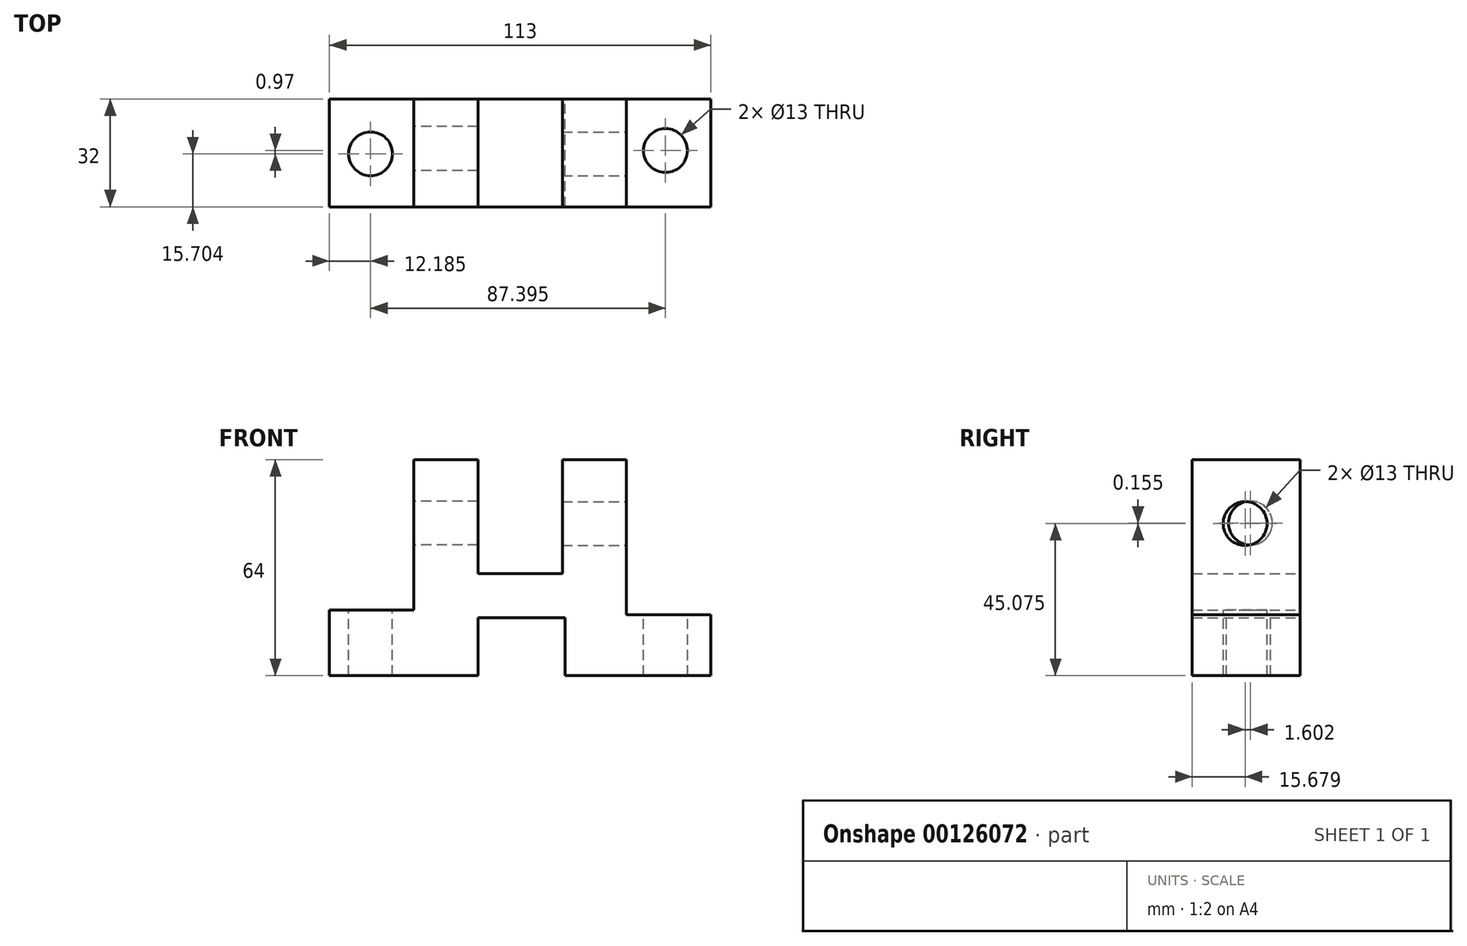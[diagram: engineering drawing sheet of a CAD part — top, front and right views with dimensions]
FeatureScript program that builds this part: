
annotation { "Feature Type Name" : "Feature", "Feature Type Description" : "" }
export const myFeature = defineFeature(function(context is Context, id is Id, definition is map)
    precondition{}
    {
        {
            var Q0;
            Q0=qCreatedBy(makeId("Front.planeOp"),FACE);
            var sketch = newSketch(context, id + "F0", { "sketchPlane" : qUnion([Q0])});
            skLineSegment(sketch, "E0", {"start": v(0, 0) * mm, "end": v(44, 0) * mm});
            skLineSegment(sketch, "E1", {"start": v(44, 0) * mm, "end": v(44, 17.17) * mm});
            skLineSegment(sketch, "E2", {"start": v(44, 17.17) * mm, "end": v(69.76, 17.17) * mm});
            skLineSegment(sketch, "E3", {"start": v(69.76, 17.17) * mm, "end": v(69.76, 0) * mm});
            skLineSegment(sketch, "E4", {"start": v(69.76, 0) * mm, "end": v(113, 0) * mm});
            skLineSegment(sketch, "E5", {"start": v(113, 0) * mm, "end": v(113, 18.09) * mm});
            skLineSegment(sketch, "E6", {"start": v(113, 18.09) * mm, "end": v(88, 18.09) * mm});
            skLineSegment(sketch, "E7", {"start": v(88, 18.09) * mm, "end": v(88, 64) * mm});
            skLineSegment(sketch, "E8", {"start": v(88, 64) * mm, "end": v(69, 64) * mm});
            skLineSegment(sketch, "E9", {"start": v(69, 64) * mm, "end": v(69, 30.17) * mm});
            skLineSegment(sketch, "E10", {"start": v(69, 30.17) * mm, "end": v(44, 30.17) * mm});
            skLineSegment(sketch, "E11", {"start": v(44, 30.17) * mm, "end": v(44, 64) * mm});
            skLineSegment(sketch, "E12", {"start": v(44, 64) * mm, "end": v(25, 64) * mm});
            skLineSegment(sketch, "E13", {"start": v(25, 64) * mm, "end": v(25, 19.49) * mm});
            skLineSegment(sketch, "E14", {"start": v(25, 19.49) * mm, "end": v(0, 19.49) * mm});
            skLineSegment(sketch, "E15", {"start": v(0, 19.49) * mm, "end": v(0, 0) * mm});
            skSolve(sketch);
        }
        {
            var Q0;
            Q0 = qSketchRegion(id + "F0", true);
            extrude(context, id + "F1", {"entities" : qUnion([Q0]), "depth" : 32 * mm});
        }
        {
            var Q0;
            Q0=makeQuery(id+"F1.opExtrude","SWEPT_FACE",FACE,{"disambiguationData":[OSD([sQuery(id+"F0.wireOp",EDGE,"E6")])]});
            var sketch = newSketch(context, id + "F2", { "sketchPlane" : qUnion([Q0])});
            skCircle(sketch, "E16", {"center": v(99.58, -15.33) * mm, "radius": 6.5 * mm});
            skSolve(sketch);
        }
        {
            var Q0;
            Q0=makeQuery(id+"F2.imprint","IMPRINT",FACE,{"disambiguationData":[TD([[makeQuery(id+"F2.imprint","IMPRINT",EDGE,{"derivedFrom":sQuery(id+"F2.wireOp",EDGE,"E16")}),1.0]])]});
            extrude(context, id + "F3", {"entities" : qUnion([Q0]), "operationType" : NewBodyOperationType.REMOVE, "oppositeDirection" : true, "depth" : 25 * mm});
        }
        {
            var Q0;
            Q0=makeQuery(id+"F1.opExtrude","SWEPT_FACE",FACE,{"disambiguationData":[OSD([sQuery(id+"F0.wireOp",EDGE,"E14")])]});
            var sketch = newSketch(context, id + "F4", { "sketchPlane" : qUnion([Q0])});
            skCircle(sketch, "E17", {"center": v(12.19, -16.3) * mm, "radius": 6.5 * mm});
            skSolve(sketch);
        }
        {
            var Q0;
            Q0=makeQuery(id+"F4.imprint","IMPRINT",FACE,{"disambiguationData":[TD([[makeQuery(id+"F4.imprint","IMPRINT",EDGE,{"derivedFrom":sQuery(id+"F4.wireOp",EDGE,"E17")}),1.0]])]});
            extrude(context, id + "F5", {"entities" : qUnion([Q0]), "operationType" : NewBodyOperationType.REMOVE, "oppositeDirection" : true, "depth" : 25 * mm});
        }
        {
            var Q0;
            Q0=makeQuery(id+"F1.opExtrude","SWEPT_FACE",FACE,{"disambiguationData":[OSD([sQuery(id+"F0.wireOp",EDGE,"E7")])]});
            var sketch = newSketch(context, id + "F6", { "sketchPlane" : qUnion([Q0])});
            skCircle(sketch, "E18", {"center": v(-16.32, 45.08) * mm, "radius": 6.5 * mm});
            skSolve(sketch);
        }
        {
            var Q0;
            Q0=makeQuery(id+"F6.imprint","IMPRINT",FACE,{"disambiguationData":[TD([[makeQuery(id+"F6.imprint","IMPRINT",EDGE,{"derivedFrom":sQuery(id+"F6.wireOp",EDGE,"E18")}),1.0]])]});
            extrude(context, id + "F7", {"entities" : qUnion([Q0]), "operationType" : NewBodyOperationType.REMOVE, "oppositeDirection" : true, "depth" : 25 * mm});
        }
        {
            var Q0;
            Q0=makeQuery(id+"F1.opExtrude","SWEPT_FACE",FACE,{"disambiguationData":[OSD([sQuery(id+"F0.wireOp",EDGE,"E13")])]});
            var sketch = newSketch(context, id + "F8", { "sketchPlane" : qUnion([Q0])});
            skCircle(sketch, "E19", {"center": v(14.72, 45.23) * mm, "radius": 6.5 * mm});
            skSolve(sketch);
        }
        {
            var Q0;
            Q0 = qSketchRegion(id + "F8", true);
            extrude(context, id + "F9", {"entities" : qUnion([Q0]), "operationType" : NewBodyOperationType.REMOVE, "oppositeDirection" : true, "depth" : 25 * mm});
        }
    });
